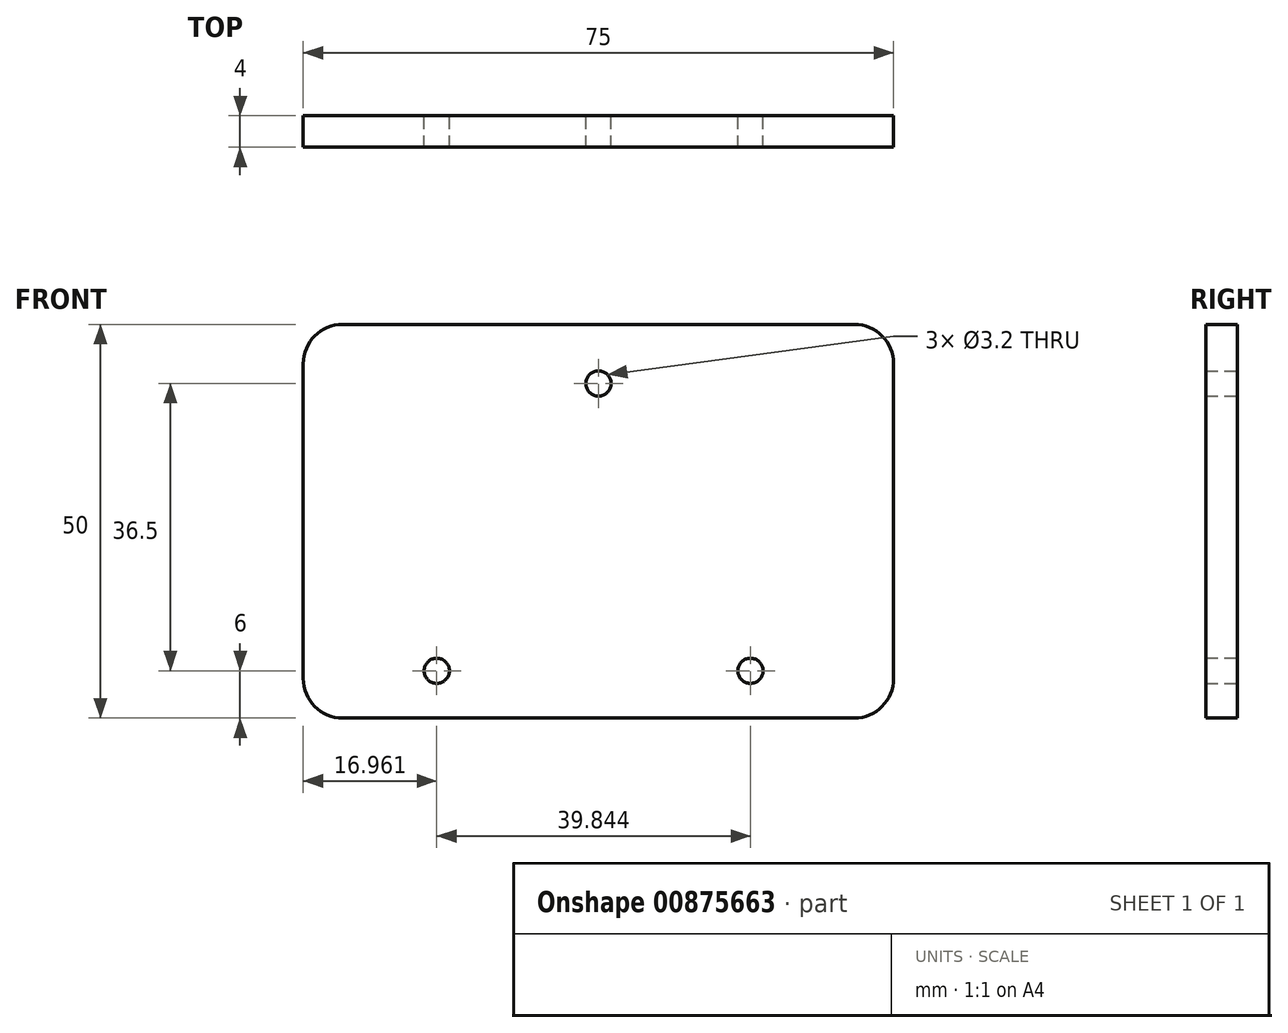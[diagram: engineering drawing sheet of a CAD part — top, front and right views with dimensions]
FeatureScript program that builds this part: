
annotation { "Feature Type Name" : "Feature", "Feature Type Description" : "" }
export const myFeature = defineFeature(function(context is Context, id is Id, definition is map)
    precondition{}
    {
        {
            var Q0;
            Q0=qCreatedBy(makeId("Front.planeOp"),FACE);
            var sketch = newSketch(context, id + "F0", { "sketchPlane" : qUnion([Q0])});
            skLineSegment(sketch, "E0.left", {"start": v(0, 0) * mm, "end": v(0, 40) * mm});
            skLineSegment(sketch, "E0.right", {"start": v(-75, 0) * mm, "end": v(-75, 40) * mm});
            skLineSegment(sketch, "E1", {"start": v(0, 20) * mm, "end": v(-75, 20) * mm, "construction": true});
            skLineSegment(sketch, "E2", {"start": v(0, 0) * mm, "end": v(0, 10) * mm, "construction": true});
            skLineSegment(sketch, "E3", {"start": v(0, 10) * mm, "end": v(-75, 10) * mm, "construction": true});
            skLineSegment(sketch, "E4", {"start": v(-75, 10) * mm, "end": v(-75, 30) * mm, "construction": true});
            skLineSegment(sketch, "E5", {"start": v(-75, 30) * mm, "end": v(0, 30) * mm, "construction": true});
            skLineSegment(sketch, "E6", {"start": v(-75, 30) * mm, "end": v(-75, 37.5) * mm, "construction": true});
            skLineSegment(sketch, "E7", {"start": v(-75, 10) * mm, "end": v(-75, 1) * mm, "construction": true});
            skLineSegment(sketch, "E8", {"start": v(-75, 0) * mm, "end": v(-75, -5) * mm});
            skLineSegment(sketch, "E9", {"start": v(-75, -5) * mm, "end": v(0, -5) * mm});
            skLineSegment(sketch, "E10", {"start": v(0, -5) * mm, "end": v(0, 0) * mm});
            skLineSegment(sketch, "E11", {"start": v(-75, 40) * mm, "end": v(-75, 45) * mm});
            skLineSegment(sketch, "E12", {"start": v(-75, 45) * mm, "end": v(0, 45) * mm});
            skLineSegment(sketch, "E13", {"start": v(0, 45) * mm, "end": v(0, 40) * mm});
            skCircle(sketch, "E14", {"center": v(-37.5, 37.5) * mm, "radius": 1.6 * mm});
            skPoint(sketch, "E14.centerSnap0", {"position": v(-37.5, 30) * mm});
            skCircle(sketch, "E15", {"center": v(-58.04, 1) * mm, "radius": 1.6 * mm});
            skCircle(sketch, "E16", {"center": v(-18.2, 1) * mm, "radius": 1.6 * mm});
            skSolve(sketch);
        }
        {
            var Q0;
            Q0=makeQuery(id+"F0.imprint","IMPRINT",FACE,{"disambiguationData":[TD([[makeQuery(id+"F0.imprint","IMPRINT",EDGE,{"derivedFrom":sQuery(id+"F0.wireOp",EDGE,"E0.left")}),1.0]])]});
            extrude(context, id + "F1", {"entities" : qUnion([Q0]), "depth" : 4 * mm, "offsetDistance" : 25 * mm});
        }
        {
            var Q0;
            Q0=makeQuery(id+"F1.opExtrude","SWEPT_EDGE",EDGE,{"disambiguationData":[OSD([sQuery(id+"F0.wireOp",EDGE,"E11"),sQuery(id+"F0.wireOp",EDGE,"E12")])]});
            var Q1;
            Q1=makeQuery(id+"F1.opExtrude","SWEPT_EDGE",EDGE,{"disambiguationData":[OSD([sQuery(id+"F0.wireOp",EDGE,"E12"),sQuery(id+"F0.wireOp",EDGE,"E13")])]});
            var Q2;
            Q2=makeQuery(id+"F1.opExtrude","SWEPT_EDGE",EDGE,{"disambiguationData":[OSD([sQuery(id+"F0.wireOp",EDGE,"E9"),sQuery(id+"F0.wireOp",EDGE,"E10")])]});
            var Q3;
            Q3=makeQuery(id+"F1.opExtrude","SWEPT_EDGE",EDGE,{"disambiguationData":[OSD([sQuery(id+"F0.wireOp",EDGE,"E8"),sQuery(id+"F0.wireOp",EDGE,"E9")])]});
            fillet(context, id + "F2", {"entities" : qUnion([Q0, Q1, Q2, Q3]), "radius" : 5 * mm, "tangentPropagation" : true, "allowEdgeOverflow" : false});
        }
    });
